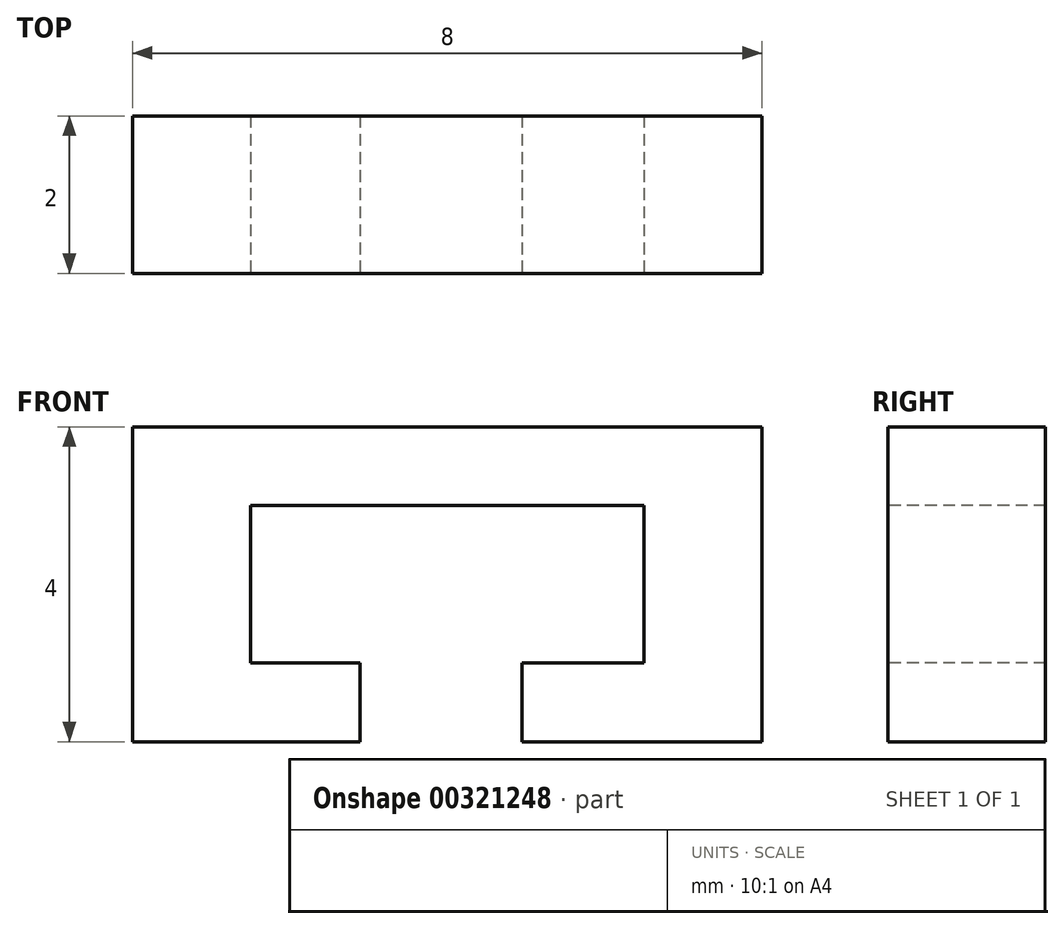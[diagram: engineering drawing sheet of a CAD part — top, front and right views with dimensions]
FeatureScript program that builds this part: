
annotation { "Feature Type Name" : "Feature", "Feature Type Description" : "" }
export const myFeature = defineFeature(function(context is Context, id is Id, definition is map)
    precondition{}
    {
        {
            var Q0;
            Q0=qCreatedBy(makeId("Front.planeOp"),FACE);
            var sketch = newSketch(context, id + "F0", { "sketchPlane" : qUnion([Q0])});
            skLineSegment(sketch, "E0.bottom", {"start": v(0, 0) * mm, "end": v(8, 0) * mm});
            skLineSegment(sketch, "E0.top", {"start": v(0, 4) * mm, "end": v(8, 4) * mm});
            skLineSegment(sketch, "E0.left", {"start": v(0, 0) * mm, "end": v(0, 4) * mm});
            skLineSegment(sketch, "E0.right", {"start": v(8, 0) * mm, "end": v(8, 4) * mm});
            skLineSegment(sketch, "E1", {"start": v(0, 0) * mm, "end": v(2.9, 0) * mm});
            skLineSegment(sketch, "E2", {"start": v(2.9, 0) * mm, "end": v(2.9, 1) * mm});
            skLineSegment(sketch, "E3", {"start": v(2.9, 1) * mm, "end": v(1.5, 1) * mm});
            skLineSegment(sketch, "E4", {"start": v(1.5, 1) * mm, "end": v(1.5, 3) * mm});
            skLineSegment(sketch, "E5", {"start": v(1.5, 3) * mm, "end": v(6.5, 3) * mm});
            skLineSegment(sketch, "E6", {"start": v(6.5, 3) * mm, "end": v(6.5, 1) * mm});
            skLineSegment(sketch, "E7", {"start": v(6.5, 1) * mm, "end": v(4.95, 1) * mm});
            skLineSegment(sketch, "E8", {"start": v(4.95, 1) * mm, "end": v(4.95, 0) * mm});
            skSolve(sketch);
        }
        {
            var Q0;
            Q0 = qSketchRegion(id + "F0", true);
            extrude(context, id + "F1", {"entities" : qUnion([Q0]), "oppositeDirection" : true, "depth" : 2 * mm});
        }
        {
            var Q0;
            {var subQ0=sQuery(id+"F0.wireOp",EDGE,"E2");Q0=makeQuery(id+"F0.imprint","IMPRINT",FACE,{"disambiguationData":[TD([[makeQuery(id+"F0.imprint","IMPRINT",EDGE,{"derivedFrom":subQ0}),-1.0]])]});}
            extrude(context, id + "F2", {"entities" : qUnion([Q0]), "operationType" : NewBodyOperationType.REMOVE, "oppositeDirection" : true, "depth" : 25 * mm});
        }
    });
